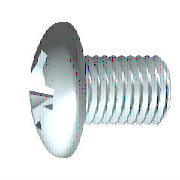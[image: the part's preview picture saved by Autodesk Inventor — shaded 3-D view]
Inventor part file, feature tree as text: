
AUTODESK INVENTOR PART (.ipt)
format: ipt  version: 2015 (Build 190159000, 159)  size: 335,360 bytes
history: native  units: mm (DEFAULTED — no unit token found)
features: other x2, extrude x2, plane x1
ambient origin geometry x7: Origin, YZ Plane, XZ Plane, X Axis, Y Axis, Z Axis, Center Point
bodies: Solid1 (feature_tree), Body (feature_tree)
feature tree (5):
  other  "IDS_WORKPLANE{1}"
  extrude  "Slot"  Depth=3.5mm
  other  "Cut"
  extrude  "Star Cut"  Depth=2.36mm
  plane  "Work Plane3"
